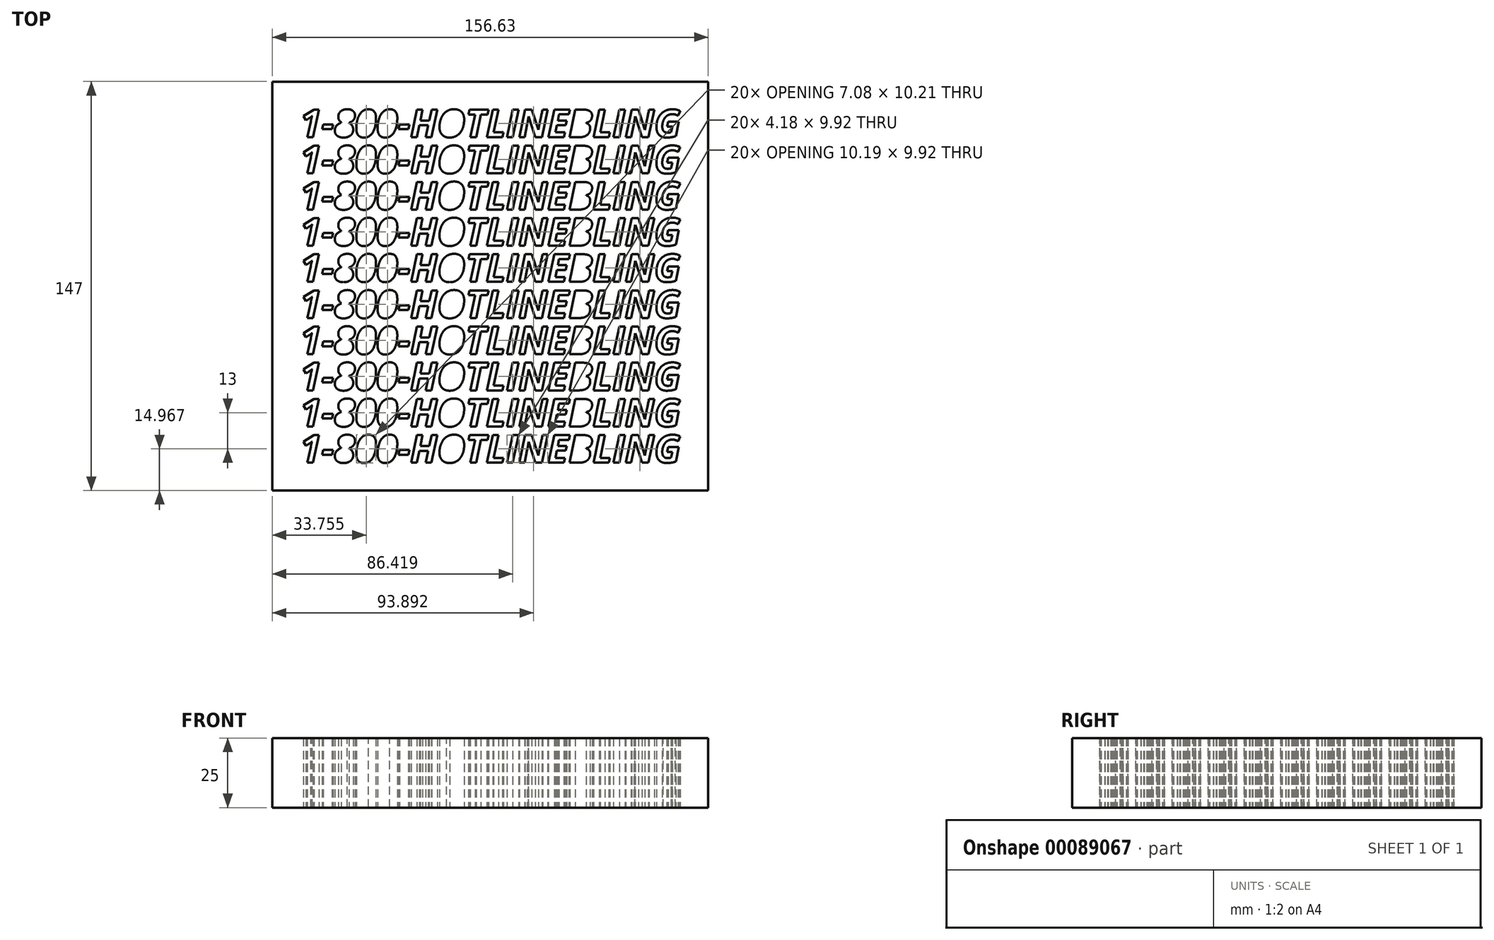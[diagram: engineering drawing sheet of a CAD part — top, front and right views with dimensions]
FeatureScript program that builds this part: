
annotation { "Feature Type Name" : "Feature", "Feature Type Description" : "" }
export const myFeature = defineFeature(function(context is Context, id is Id, definition is map)
    precondition{}
    {
        {
            var Q0;
            Q0=qCreatedBy(makeId("Top.planeOp"),FACE);
            var sketch = newSketch(context, id + "F0", { "sketchPlane" : qUnion([Q0])});
            skText(sketch, "E0", { "text": "1-800-HOTLINEBLING", "fontName": "OpenSans-BoldItalic.ttf"});
            skText(sketch, "E1", { "text": "1-800-HOTLINEBLING", "fontName": "OpenSans-BoldItalic.ttf"});
            skText(sketch, "E2", { "text": "1-800-HOTLINEBLING", "fontName": "OpenSans-BoldItalic.ttf"});
            skText(sketch, "E3", { "text": "1-800-HOTLINEBLING", "fontName": "OpenSans-BoldItalic.ttf"});
            skText(sketch, "E4", { "text": "1-800-HOTLINEBLING", "fontName": "OpenSans-BoldItalic.ttf"});
            skText(sketch, "E5", { "text": "1-800-HOTLINEBLING", "fontName": "OpenSans-BoldItalic.ttf"});
            skText(sketch, "E6", { "text": "1-800-HOTLINEBLING", "fontName": "OpenSans-BoldItalic.ttf"});
            skText(sketch, "E7", { "text": "1-800-HOTLINEBLING", "fontName": "OpenSans-BoldItalic.ttf"});
            skText(sketch, "E8", { "text": "1-800-HOTLINEBLING", "fontName": "OpenSans-BoldItalic.ttf"});
            skText(sketch, "E9", { "text": "1-800-HOTLINEBLING", "fontName": "OpenSans-BoldItalic.ttf"});
            skLineSegment(sketch, "E10.bottom", {"start": v(8.11, 30.4) * mm, "end": v(144.74, 30.4) * mm});
            skLineSegment(sketch, "E10.top", {"start": v(8.11, -96.6) * mm, "end": v(144.74, -96.6) * mm});
            skLineSegment(sketch, "E10.left", {"start": v(8.11, 30.4) * mm, "end": v(8.11, -96.6) * mm});
            skLineSegment(sketch, "E10.right", {"start": v(144.74, 30.4) * mm, "end": v(144.74, -96.6) * mm});
            skLineSegment(sketch, "E11.bottom", {"start": v(-1.89, 30.4) * mm, "end": v(8.11, 30.4) * mm});
            skLineSegment(sketch, "E11.top", {"start": v(-1.89, -96.6) * mm, "end": v(8.11, -96.6) * mm});
            skLineSegment(sketch, "E11.left", {"start": v(-1.89, 30.4) * mm, "end": v(-1.89, -96.6) * mm});
            skLineSegment(sketch, "E12.bottom", {"start": v(-1.89, 40.4) * mm, "end": v(144.74, 40.4) * mm});
            skLineSegment(sketch, "E12.top", {"start": v(-1.89, 30.4) * mm, "end": v(144.74, 30.4) * mm});
            skLineSegment(sketch, "E12.left", {"start": v(-1.89, 40.4) * mm, "end": v(-1.89, 30.4) * mm});
            skLineSegment(sketch, "E12.right", {"start": v(144.74, 40.4) * mm, "end": v(144.74, 30.4) * mm});
            skLineSegment(sketch, "E13.bottom", {"start": v(154.74, 40.4) * mm, "end": v(144.74, 40.4) * mm});
            skLineSegment(sketch, "E13.top", {"start": v(154.74, -96.6) * mm, "end": v(144.74, -96.6) * mm});
            skLineSegment(sketch, "E13.left", {"start": v(154.74, 40.4) * mm, "end": v(154.74, -96.6) * mm});
            skLineSegment(sketch, "E13.right", {"start": v(144.74, 40.4) * mm, "end": v(144.74, -96.6) * mm});
            skLineSegment(sketch, "E14.bottom", {"start": v(154.74, -106.6) * mm, "end": v(-1.89, -106.6) * mm});
            skLineSegment(sketch, "E14.top", {"start": v(154.74, -96.6) * mm, "end": v(-1.89, -96.6) * mm});
            skLineSegment(sketch, "E14.left", {"start": v(154.74, -106.6) * mm, "end": v(154.74, -96.6) * mm});
            skLineSegment(sketch, "E14.right", {"start": v(-1.89, -106.6) * mm, "end": v(-1.89, -96.6) * mm});
            const initialGuessF0  = {"E0": [0.00811, 0.0204, 1, 0, 0.01], "E1": [0.00811, 0.0074, 1, 0, 0.01], "E2": [0.00811, -0.0056, 1, 0, 0.01], "E3": [0.00811, -0.0186, 1, 0, 0.01], "E4": [0.00811, -0.0316, 1, 0, 0.01], "E5": [0.00811, -0.0446, 1, 0, 0.01], "E6": [0.00811, -0.0576, 1, 0, 0.01], "E7": [0.00811, -0.0706, 1, 0, 0.01], "E8": [0.00811, -0.0836, 1, 0, 0.01], "E9": [0.00811, -0.0966, 1, 0, 0.01]};
            skSetInitialGuess(sketch, initialGuessF0);
            skSolve(sketch);
        }
        {
            var Q0;
            Q0 = qSketchRegion(id + "F0", true);
            var Q1;
            Q1=makeQuery(id+"F0.imprint","IMPRINT",FACE,{"disambiguationData":[TD([[makeQuery(id+"F0.imprint","IMPRINT",EDGE,{"derivedFrom":sQuery(id+"F0.wireOp",EDGE,"E0.sketch_text.stroke-0")}),1.0]])]});
            var Q2;
            {var subQ1=sQuery(id+"F0.wireOp",EDGE,"E9.sketch_text.stroke-134");Q2=makeQuery(id+"F0.imprint","IMPRINT",FACE,{"disambiguationData":[TD([[makeQuery(id+"F0.imprint","IMPRINT",EDGE,{"derivedFrom":subQ1}),1.0]])]});}
            var Q3;
            {var subQ0=sQuery(id+"F0.wireOp",EDGE,"E9.sketch_text.stroke-84");Q3=makeQuery(id+"F0.imprint","IMPRINT",FACE,{"disambiguationData":[TD([[makeQuery(id+"F0.imprint","IMPRINT",EDGE,{"derivedFrom":subQ0}),1.0]])]});}
            var Q4;
            {var subQ0=sQuery(id+"F0.wireOp",EDGE,"E9.sketch_text.stroke-195");Q4=makeQuery(id+"F0.imprint","IMPRINT",FACE,{"disambiguationData":[TD([[makeQuery(id+"F0.imprint","IMPRINT",EDGE,{"derivedFrom":subQ0}),1.0]])]});}
            var Q5;
            Q5=makeQuery(id+"F0.imprint","IMPRINT",FACE,{"disambiguationData":[TD([[makeQuery(id+"F0.imprint","IMPRINT",EDGE,{"derivedFrom":sQuery(id+"F0.wireOp",EDGE,"E9.sketch_text.stroke-209")}),1.0]])]});
            extrude(context, id + "F1", {"entities" : qUnion([Q0, Q1, Q2, Q3, Q4, Q5]), "depth" : 25 * mm});
        }
    });
